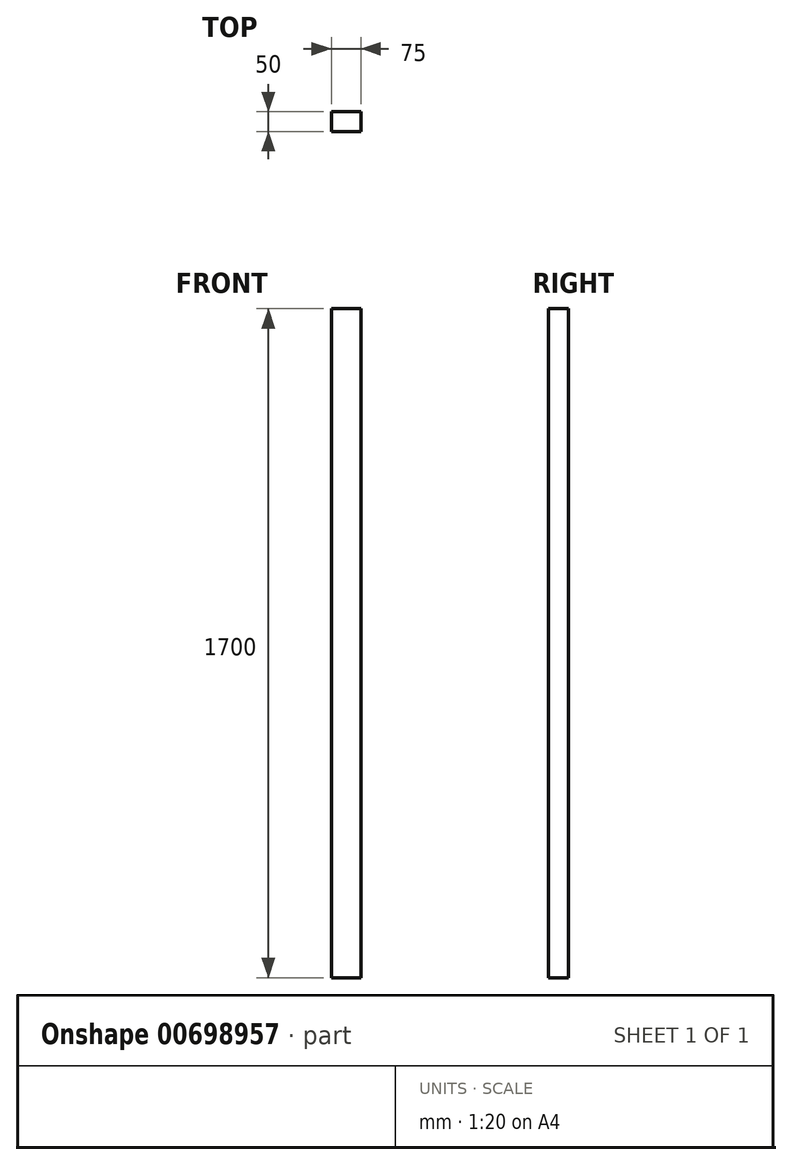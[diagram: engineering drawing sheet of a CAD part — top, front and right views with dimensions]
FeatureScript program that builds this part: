
annotation { "Feature Type Name" : "Feature", "Feature Type Description" : "" }
export const myFeature = defineFeature(function(context is Context, id is Id, definition is map)
    precondition{}
    {
        {
            var Q0;
            Q0=qCreatedBy(makeId("Front.planeOp"),FACE);
            var sketch = newSketch(context, id + "F0", { "sketchPlane" : qUnion([Q0])});
            skLineSegment(sketch, "E0.bottom", {"start": v(-37.5, -850) * mm, "end": v(37.5, -850) * mm});
            skLineSegment(sketch, "E0.top", {"start": v(-37.5, 850) * mm, "end": v(37.5, 850) * mm});
            skLineSegment(sketch, "E0.left", {"start": v(-37.5, -850) * mm, "end": v(-37.5, 850) * mm});
            skLineSegment(sketch, "E0.right", {"start": v(37.5, -850) * mm, "end": v(37.5, 850) * mm});
            skLineSegment(sketch, "E1", {"start": v(0, 0) * mm, "end": v(0, -850) * mm, "construction": true});
            skLineSegment(sketch, "E2", {"start": v(0, 0) * mm, "end": v(37.5, 0) * mm, "construction": true});
            skSolve(sketch);
        }
        {
            var Q0;
            Q0 = qSketchRegion(id + "F0", true);
            extrude(context, id + "F1", {"entities" : qUnion([Q0]), "depth" : 50 * mm, "offsetDistance" : 25 * mm, "symmetric" : true});
        }
    });
